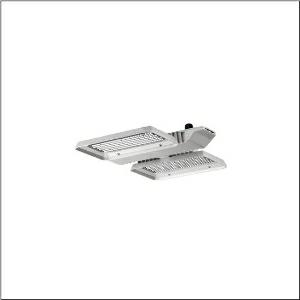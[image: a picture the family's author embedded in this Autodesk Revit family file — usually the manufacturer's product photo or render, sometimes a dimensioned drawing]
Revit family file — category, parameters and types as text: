
# Revit family: highbay_21_51hlasd14fgb
name_source: partatom
category: Lighting Fixtures
units: mm (PartAtom-declared; Revit-internal decimal feet)

## family parameters
Cut with Voids When Loaded = No
Host = Face
Light Source = No
Part Type = Normal
Room Calculation Point = No
Round Connector Dimension = Use Diameter
Shared = No

## types (1)
- --- (1 x LED, 13800 lm, 85.5 W, 4000K)
    Apparent Load = 86 VA
    CIE Flux Codes = 89 96 99 100 100
    Color Rendering = 80
    Color Temperature = 4000K
    Default Elevation = 1800 mm
    Description = Highbay 21, LED high bay luminaire, primary light control with lens, of PMMA, light emission: direct distribution, primary light characteristic: symmetric, installation type: suspended mounting, for 1x 2 x LED rated luminous flux: 13.800 lm, light colour: 840, colour temperature: 4000K, control gear: ECG DALI, with terminal, 5-pole, max. 2.5mm², mains connection: 230..240V, AC, 50/60Hz, rated input power: 86W, LED unit, of diecast aluminium, unplated, bead blasted, silver, length: 470 mm, width: 500 mm, height: 65mm, housing, of diecast aluminium, uncoated, bead blasted, silver, protection rating (complete): IP20, insulation class (complete): insulation class I (protective earthing), certification: CE, ENEC, VDE, protection symbol: D, ball protection: ball impact resistant according to DIN VDE 0710 part 13 (with chain suspension), permissible ambient temperature for indoor applications: -35..+45°C, corresponds to IFS (International Featured Standards) requirements for safety and quality in the food industry, reducing of maximum allowable ambient temperature of 5°C with ceiling mounting, packaging unit: 1 piece
    Height = 95 mm
    Lamp = 1 x LED
    Lamp Light Flux = 13800 lm
    Lamp Power = 85.5 W
    Lamp count = 1
    Length = 468 mm
    Luminous efficacy = 161 lm/W
    Manufacturer = Siteco
    ModVariant = No
    Model = 51HLASD14FGB
    Mounting Place = Ceiling
    Mounting Type = Pendant
    Number of Poles = 1
    OnlyDefault = Yes
    Power Factor = 1
    Product Name = Highbay 21
    Product group = LED high bay luminaire
    ProductGroupID = 903
    Protection Class = Protection class I
    Protection Degree = IP 20
    RLX_Detail_Level = 1
    RlxData = <blob elided: 53625 chars, md5=c6f968ae>
    Socket = socket
    Standby Power = 0 W
    System Light Flux = 13800 lm
    System Power = 86 W
    Type Comments = factory setting: luminous flux: 100 % | dim-lin: 254 | 491 mA
    Type Image = l_1006019.jpg
    URL = http://relux.com
    VarID = @adj_135729
    Voltage = 0 V
    Weight = 0.00 kg
    Width = 501 mm

## geometry (parser evidence)
native form markers: Blend x4, Sweep x10
no freeform markers — native parametric forms only
